# Revit family: P2078-09
name_source: partatom
category: Lighting Fixtures
revit_build: Autodesk Revit 2014 (Build: 20130308_1515(x64)
units: mm (PartAtom-declared; Revit-internal decimal feet)

## types (1)
- P2078-09
    Apparent Load = 100 VA
    Assembly Code = D5020200
    Connector Description = Lighting Connector
    Default Elevation = 48"
    Description = Invite the beauty of light into your home with this Brushed Nickel two-light bath fixture. Invite provides a welcoming silhouette with a unique shade comprised of an inner glass globe encircled by a translucent sheer Mylar shade. The rich, layering effect creates a dreamy look that is both elegant and modern. Offered as a complete collection, the Invite styling can be carried throughout your home or as a focal style in a special room.
    Features = Brushed Nickel finish.
Inner glass globe encircled by a translucent sheer mylar shade.
Features a welcoming silhouette.
Rich, layering effect creates a dreamy look.
    Fixture distribution = Direct
    Glass = Hubbell - Glass
    Height = 7 3/8"
    Housing Material = Paint - Hubbell - Light Silver
    Lamp = A-19
    Load Classification = Lighting
    Manufacturer = Progress Lighting
    Model = P2078-09
    Power Factor = 1
    Product Documentation Link = https://hubbellcdn.com
    Product Link = https://www.hubbell.com
    URL = https://www.hubbell.com
    Voltage = 120 V
    Warranty = 5 years Warranty
    Wattage Comments = 100W
    Watts = 100 W
    Width = 14 1/2"

## geometry (parser evidence)
native form markers: Sweep x6
no freeform markers — native parametric forms only
